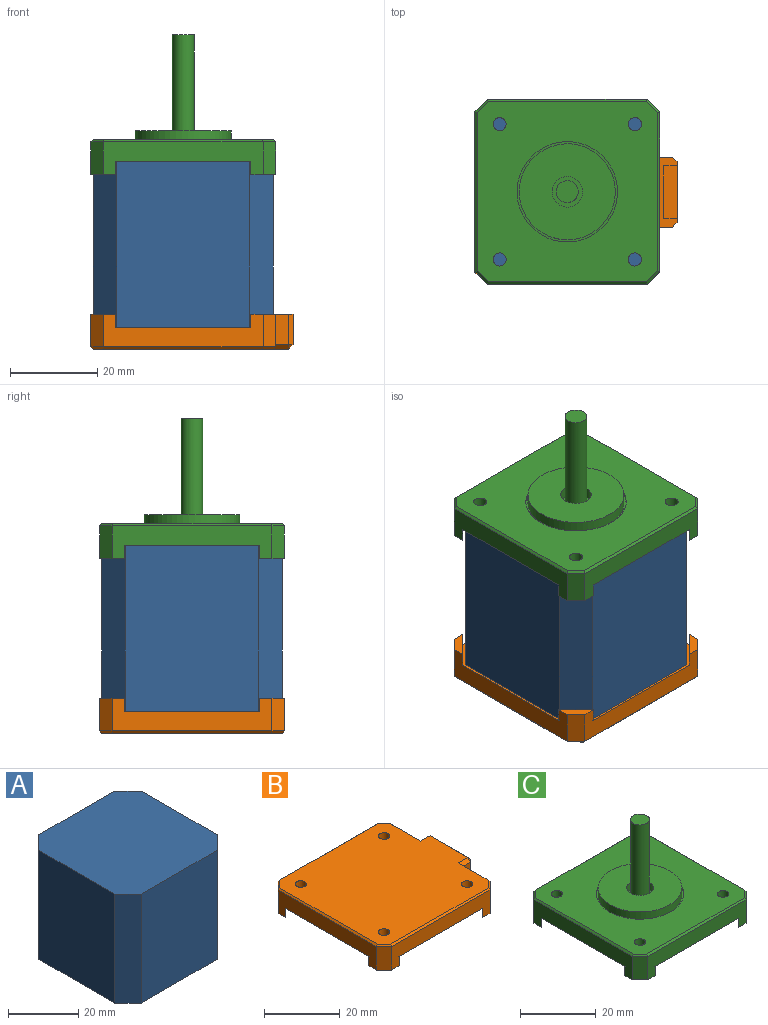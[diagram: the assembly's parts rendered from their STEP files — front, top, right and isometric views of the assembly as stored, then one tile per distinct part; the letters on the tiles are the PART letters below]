
ASSEMBLY  parts=3 mates=2
PART A: 10 faces, bbox 41.3x41.3x38 mm
  f0: plane 38x30.57mm, normal (0,1,0), area 1161.7mm2, adj f1,f7,f8,f9
  f1: plane 38x5.36mm, normal (-0.71,0.71,0), area 288.3mm2, adj f0,f2,f8,f9
  f2: plane 38x30.57mm, normal (-1,0,0), area 1161.7mm2, adj f1,f3,f8,f9
  f3: plane 38x5.36mm, normal (-0.71,-0.71,0), area 288.3mm2, adj f2,f4,f8,f9
  f4: plane 38x30.57mm, normal (0,-1,0), area 1161.7mm2, adj f3,f5,f8,f9
  f5: plane 38x5.36mm, normal (0.71,-0.71,0), area 288.3mm2, adj f4,f6,f8,f9
  f6: plane 38x30.57mm, normal (1,0,0), area 1161.7mm2, adj f5,f7,f8,f9
  f7: plane 38x5.36mm, normal (0.71,0.71,0), area 288.3mm2, adj f0,f6,f8,f9
  f8: plane 41.3x41.3mm, normal (0,0,1), area 1648.1mm2, adj f0,f1,f2,f3,f4,f5,f6,f7
  f9: plane 41.3x41.3mm, normal (0,0,-1), area 1648.1mm2, adj f0,f1,f2,f3,f4,f5,f6,f7
PART B: 48 faces, bbox 46.3x42.3x8 mm
  f0: plane 42.3x42.3mm, normal (0,0,-1), area 1697mm2, adj f1,f3,f5,f7,f9,f12,f13,f14
  f1: plane 10.82x7.5mm, normal (1,0,0), area 55.1mm2, adj f0,f2,f15,f22,f23,f32,f39
  f2: plane 7.5x2.83mm, normal (0.71,0.71,0), area 30mm2, adj f1,f3,f23,f40
  f3: plane 36.64x7.5mm, normal (0,1,0), area 181.9mm2, adj f0,f2,f4,f20,f21,f22,f23,f41
  f4: plane 7.5x2.83mm, normal (-0.71,0.71,0), area 30mm2, adj f3,f5,f21,f42
  f5: plane 36.64x7.5mm, normal (-1,0,0), area 181.9mm2, adj f0,f4,f6,f18,f19,f20,f21,f43
  f6: plane 7.5x2.83mm, normal (-0.71,-0.71,0), area 30mm2, adj f5,f7,f19,f44
  f7: plane 36.64x7.5mm, normal (0,-1,0), area 181.9mm2, adj f0,f6,f8,f18,f19,f29,f30,f45
  f8: plane 7.5x2.83mm, normal (0.71,-0.71,0), area 30mm2, adj f7,f9,f30,f46
  f9: plane 10.82x7.5mm, normal (1,0,0), area 55.1mm2, adj f0,f8,f10,f29,f30,f35,f47
  f10: plane 7x3mm, normal (0,-1,0), area 21mm2, adj f9,f25,f28,f35,f38
  f11: plane 14x7mm, normal (1,0,0), area 38mm2, adj f24,f26,f28,f31,f33,f36,f38
  f12: cylinder r=1.5mm len=5mm, axis (0,0,-1), area 47.1mm2, adj f0,f17
  f13: cylinder r=1.5mm len=5mm, axis (0,0,-1), area 47.1mm2, adj f0,f17
  f14: cylinder r=1.5mm len=5mm, axis (0,0,-1), area 47.1mm2, adj f0,f17
  f15: plane 7x3mm, normal (0,1,0), area 21mm2, adj f1,f25,f28,f32,f33
  f16: cylinder r=1.5mm len=5mm, axis (0,0,-1), area 47.1mm2, adj f0,f17
  f17: plane 44.8x41.3mm, normal (0,0,1), area 1713.6mm2, adj f12,f13,f14,f16,f32,f35,f36,f39
  f18: plane 5.66x5.66mm, normal (0.71,0.71,0), area 24mm2, adj f0,f5,f7,f19
  f19: plane 5.66x5.66mm, normal (0,0,-1), area 12mm2, adj f5,f6,f7,f18
  f20: plane 5.66x5.66mm, normal (0.71,-0.71,0), area 24mm2, adj f0,f3,f5,f21
  f21: plane 5.66x5.66mm, normal (0,0,-1), area 12mm2, adj f3,f4,f5,f20
  f22: plane 5.66x5.66mm, normal (-0.71,-0.71,0), area 24mm2, adj f0,f1,f3,f23
  f23: plane 5.66x5.66mm, normal (0,0,-1), area 12mm2, adj f1,f2,f3,f22
  f24: plane 5x3mm, normal (0,-1,0), area 15mm2, adj f11,f27,f28,f31
  f25: plane 16x3mm, normal (-1,0,0), area 48mm2, adj f0,f10,f15,f28
  f26: plane 5x3mm, normal (0,1,0), area 15mm2, adj f11,f27,f28,f31
  f27: plane 12x5mm, normal (1,0,0), area 60mm2, adj f24,f26,f28,f31
  f28: plane 16x4mm, normal (0,0,-1), area 27mm2, adj f10,f11,f15,f24,f25,f26,f27,f33
  f29: plane 5.66x5.66mm, normal (-0.71,0.71,0), area 24mm2, adj f0,f7,f9,f30
  f30: plane 5.66x5.66mm, normal (0,0,-1), area 12mm2, adj f7,f8,f9,f29
  f31: plane 12x3mm, normal (0,0,-1), area 36mm2, adj f11,f24,f26,f27
  f32: plane 3.5x1mm, normal (0,0.71,0.71), area 4.4mm2, adj f1,f15,f17,f34,f39
  f33: plane 7x1mm, normal (0.71,0.71,0), area 9.9mm2, adj f11,f15,f28,f34
  f34: plane 1x1mm, normal (0.58,0.58,0.58), area 0.9mm2, adj f32,f33,f36
  f35: plane 3.5x1mm, normal (0,-0.71,0.71), area 4.4mm2, adj f9,f10,f17,f37,f47
  f36: plane 14x1mm, normal (0.71,0,0.71), area 19.8mm2, adj f11,f17,f34,f37
  f37: plane 1x1mm, normal (0.58,-0.58,0.58), area 0.9mm2, adj f35,f36,f38
  f38: plane 7x1mm, normal (0.71,-0.71,0), area 9.9mm2, adj f10,f11,f28,f37
  f39: plane 11.32x0.5mm, normal (0.71,0,0.71), area 7.8mm2, adj f1,f17,f32,f40
  f40: plane 3.04x3.04mm, normal (0.5,0.5,0.71), area 2.7mm2, adj f2,f17,f39,f41
  f41: plane 36.64x0.5mm, normal (0,0.71,0.71), area 25.8mm2, adj f3,f17,f40,f42
  f42: plane 3.04x3.04mm, normal (-0.5,0.5,0.71), area 2.7mm2, adj f4,f17,f41,f43
  f43: plane 36.64x0.5mm, normal (-0.71,0,0.71), area 25.8mm2, adj f5,f17,f42,f44
  f44: plane 3.04x3.04mm, normal (-0.5,-0.5,0.71), area 2.7mm2, adj f6,f17,f43,f45
  f45: plane 36.64x0.5mm, normal (0,-0.71,0.71), area 25.8mm2, adj f7,f17,f44,f46
  f46: plane 3.04x3.04mm, normal (0.5,-0.5,0.71), area 2.7mm2, adj f8,f17,f45,f47
  f47: plane 11.32x0.5mm, normal (0.71,0,0.71), area 7.8mm2, adj f9,f17,f35,f46
PART C: 38 faces, bbox 42.3x42.3x32 mm
  f0: plane 36.64x7.5mm, normal (-1,0,0), area 181.9mm2, adj f1,f10,f13,f14,f15,f20,f21,f32
  f1: plane 7.5x2.83mm, normal (-0.71,-0.71,0), area 30mm2, adj f0,f2,f15,f34
  f2: plane 36.64x7.5mm, normal (0,-1,0), area 181.9mm2, adj f1,f3,f13,f14,f15,f16,f17,f36
  f3: plane 7.5x2.83mm, normal (0.71,-0.71,0), area 30mm2, adj f2,f4,f17,f37
  f4: plane 36.64x7.5mm, normal (1,0,0), area 181.9mm2, adj f3,f5,f13,f16,f17,f18,f19,f35
  f5: plane 7.5x2.83mm, normal (0.71,0.71,0), area 30mm2, adj f4,f6,f19,f33
  f6: plane 36.64x7.5mm, normal (0,1,0), area 181.9mm2, adj f5,f10,f13,f18,f19,f20,f21,f31
  f7: cylinder r=1.5mm len=5mm, axis (0,0,-1), area 47.1mm2, adj f12,f13
  f8: cylinder r=1.5mm len=5mm, axis (0,0,-1), area 47.1mm2, adj f12,f13
  f9: cylinder r=1.5mm len=5mm, axis (0,0,-1), area 47.1mm2, adj f12,f13
  f10: plane 7.5x2.83mm, normal (-0.71,0.71,0), area 30mm2, adj f0,f6,f21,f30
  f11: cylinder r=1.5mm len=5mm, axis (0,0,-1), area 47.1mm2, adj f12,f13
  f12: plane 41.3x41.3mm, normal (0,0,1), area 1249.1mm2, adj f7,f8,f9,f11,f23,f30,f31,f32
  f13: plane 42.3x42.3mm, normal (0,0,-1), area 1697mm2, adj f0,f2,f4,f6,f7,f8,f9,f11
  f14: plane 5.66x5.66mm, normal (0.71,0.71,0), area 24mm2, adj f0,f2,f13,f15
  f15: plane 5.66x5.66mm, normal (0,0,-1), area 12mm2, adj f0,f1,f2,f14
  f16: plane 5.66x5.66mm, normal (-0.71,0.71,0), area 24mm2, adj f2,f4,f13,f17
  f17: plane 5.66x5.66mm, normal (0,0,-1), area 12mm2, adj f2,f3,f4,f16
  f18: plane 5.66x5.66mm, normal (-0.71,-0.71,0), area 24mm2, adj f4,f6,f13,f19
  f19: plane 5.66x5.66mm, normal (0,0,-1), area 12mm2, adj f4,f5,f6,f18
  f20: plane 5.66x5.66mm, normal (0.71,-0.71,0), area 24mm2, adj f0,f6,f13,f21
  f21: plane 5.66x5.66mm, normal (0,0,-1), area 12mm2, adj f0,f6,f10,f20
  f22: cylinder r=11mm len=22mm, axis (0,0,-1), area 172.8mm2, adj f24,f25
  f23: cylinder r=11.5mm len=23mm, axis (0,0,-1), area 36.1mm2, adj f12,f24
  f24: plane 23x23mm, normal (0,0,1), area 35.3mm2, adj f22,f23
  f25: plane 22x22mm, normal (0,0,1), area 341.6mm2, adj f22,f27
  f26: cylinder r=2.5mm len=24.5mm, axis (0,0,-1), area 384.8mm2, adj f28,f29
  f27: cylinder r=3.5mm len=7mm, axis (0,0,-1), area 55mm2, adj f25,f28
  f28: plane 7x7mm, normal (0,0,1), area 18.8mm2, adj f26,f27
  f29: plane 5x5mm, normal (0,0,1), area 19.6mm2, adj f26
  f30: plane 3.04x3.04mm, normal (-0.5,0.5,0.71), area 2.7mm2, adj f10,f12,f31,f32
  f31: plane 36.64x0.5mm, normal (0,0.71,0.71), area 25.8mm2, adj f6,f12,f30,f33
  f32: plane 36.64x0.5mm, normal (-0.71,0,0.71), area 25.8mm2, adj f0,f12,f30,f34
  f33: plane 3.04x3.04mm, normal (0.5,0.5,0.71), area 2.7mm2, adj f5,f12,f31,f35
  f34: plane 3.04x3.04mm, normal (-0.5,-0.5,0.71), area 2.7mm2, adj f1,f12,f32,f36
  f35: plane 36.64x0.5mm, normal (0.71,0,0.71), area 25.8mm2, adj f4,f12,f33,f37
  f36: plane 36.64x0.5mm, normal (0,-0.71,0.71), area 25.8mm2, adj f2,f12,f34,f37
  f37: plane 3.04x3.04mm, normal (0.5,-0.5,0.71), area 2.7mm2, adj f3,f12,f35,f36
PLACE A t=(-62.3,-126.9,-38)mm
PLACE B rot(axis=(1,0,0),180deg) t=(0,104.6,-38)mm
PLACE C at identity fixed
MATE fastened B.f0 <-> A.f9  axis (0,0,1) through (0,0,-38)mm
MATE fastened C.f23 <-> A.f8  axis (0,0,-1) through (0,0,0)mm
